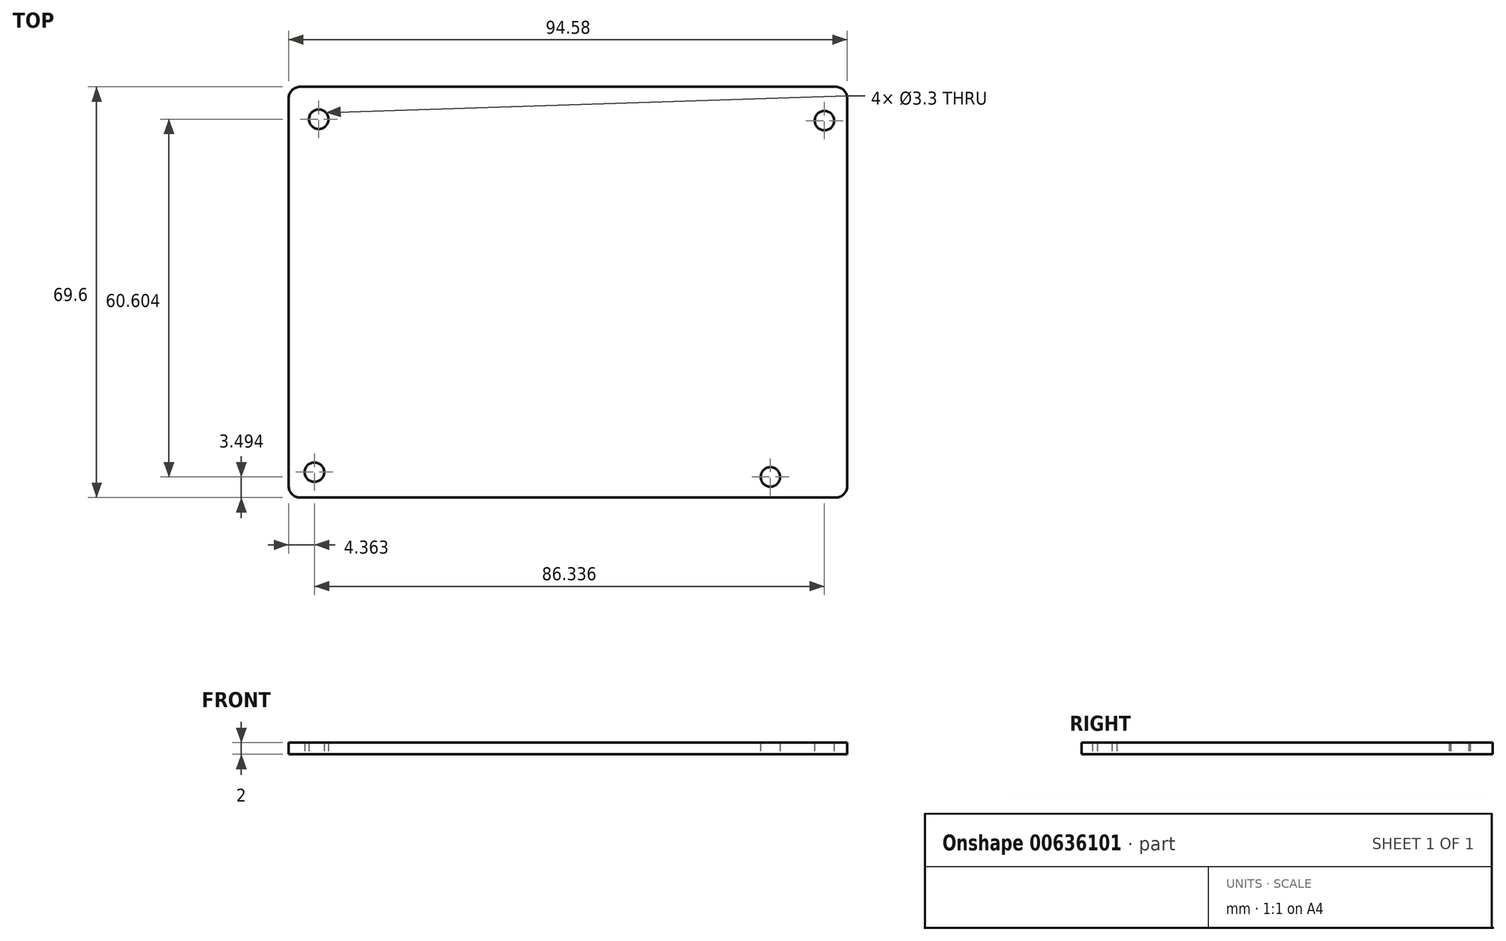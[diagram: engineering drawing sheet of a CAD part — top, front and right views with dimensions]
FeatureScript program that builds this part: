
annotation { "Feature Type Name" : "Feature", "Feature Type Description" : "" }
export const myFeature = defineFeature(function(context is Context, id is Id, definition is map)
    precondition{}
    {
        {
            var Q0;
            Q0=qCreatedBy(makeId("Top.planeOp"),FACE);
            var sketch = newSketch(context, id + "F0", { "sketchPlane" : qUnion([Q0])});
            skLineSegment(sketch, "E0.bottom", {"start": v(45.29, -32.8) * mm, "end": v(-45.29, -32.8) * mm});
            skLineSegment(sketch, "E0.top", {"start": v(45.29, 32.8) * mm, "end": v(-45.29, 32.8) * mm});
            skLineSegment(sketch, "E0.left", {"start": v(45.29, -32.8) * mm, "end": v(45.29, 32.8) * mm});
            skLineSegment(sketch, "E0.right", {"start": v(-45.29, -32.8) * mm, "end": v(-45.29, 32.8) * mm});
            skPoint(sketch, "E0.middle", {"position": v(0, 0) * mm});
            skCircle(sketch, "E1", {"center": v(-42.93, -30.5) * mm, "radius": 1.65 * mm});
            skCircle(sketch, "E2", {"center": v(-42.19, 29.3) * mm, "radius": 1.65 * mm});
            skCircle(sketch, "E3", {"center": v(43.4, 29.07) * mm, "radius": 1.65 * mm});
            skCircle(sketch, "E4", {"center": v(34.27, -31.3) * mm, "radius": 1.65 * mm});
            skLineSegment(sketch, "E5.0", {"start": v(47.29, 34.8) * mm, "end": v(-47.29, 34.8) * mm});
            skLineSegment(sketch, "E5.1", {"start": v(47.29, -34.8) * mm, "end": v(47.29, 34.8) * mm});
            skLineSegment(sketch, "E5.2", {"start": v(47.29, -34.8) * mm, "end": v(-47.29, -34.8) * mm});
            skLineSegment(sketch, "E5.3", {"start": v(-47.29, -34.8) * mm, "end": v(-47.29, 34.8) * mm});
            skSolve(sketch);
        }
        {
            var Q0;
            Q0 = qSketchRegion(id + "F0", true);
            var Q1;
            Q1=makeQuery(id+"F0.imprint","IMPRINT",FACE,{"disambiguationData":[TD([[makeQuery(id+"F0.imprint","IMPRINT",EDGE,{"derivedFrom":sQuery(id+"F0.wireOp",EDGE,"E0.top")}),1.0]])]});
            extrude(context, id + "F1", {"entities" : qUnion([Q0, Q1]), "depth" : 2 * mm, "offsetDistance" : 25 * mm});
        }
        {
            var Q0;
            Q0=makeQuery(id+"F1.opExtrude","SWEPT_EDGE",EDGE,{"disambiguationData":[OSD([sQuery(id+"F0.wireOp",EDGE,"E5.2"),sQuery(id+"F0.wireOp",EDGE,"E5.3")])]});
            var Q1;
            Q1=makeQuery(id+"F1.opExtrude","SWEPT_EDGE",EDGE,{"disambiguationData":[OSD([sQuery(id+"F0.wireOp",EDGE,"E5.0"),sQuery(id+"F0.wireOp",EDGE,"E5.3")])]});
            var Q2;
            Q2=makeQuery(id+"F1.opExtrude","SWEPT_EDGE",EDGE,{"disambiguationData":[OSD([sQuery(id+"F0.wireOp",EDGE,"E5.1"),sQuery(id+"F0.wireOp",EDGE,"E5.2")])]});
            var Q3;
            Q3=makeQuery(id+"F1.opExtrude","SWEPT_EDGE",EDGE,{"disambiguationData":[OSD([sQuery(id+"F0.wireOp",EDGE,"E5.0"),sQuery(id+"F0.wireOp",EDGE,"E5.1")])]});
            fillet(context, id + "F2", {"entities" : qUnion([Q0, Q1, Q2, Q3]), "radius" : 2 * mm, "tangentPropagation" : true, "allowEdgeOverflow" : false});
        }
    });
